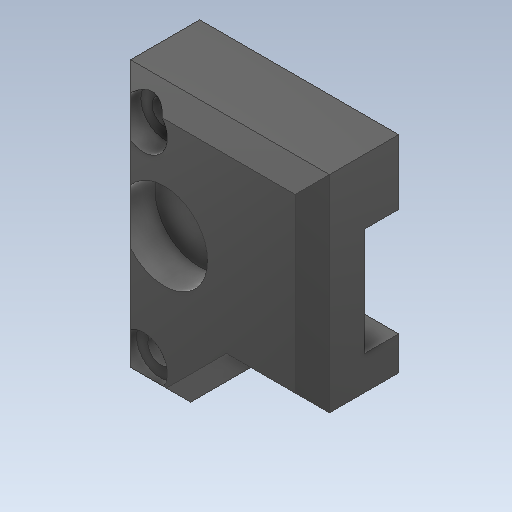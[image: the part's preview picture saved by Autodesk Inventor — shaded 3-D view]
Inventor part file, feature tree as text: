
AUTODESK INVENTOR PART (.ipt)
format: ipt  version: 2020 (Build 240168000, 168)  size: 249,856 bytes
history: native  units: in
note: dims shown in document units (in); Inventor stores cm internally (conversion verified against a paired STEP export)
features: sketch x30, other x3, plane x1
ambient origin geometry x8: Origin, YZ Plane, XZ Plane, XY Plane, X Axis, Y Axis, Z Axis, Center Point
bodies: Solid1 (feature_tree)
feature tree (34):
  other  "FermurSupportSup.ipt"
  other  "Solid1::FermurSupportSup.ipt"
  other  "TaggingFeature1"
  sketch  "Sketch1"  dims[d0=0.3937in]
  sketch  "Sketch2"
  sketch  "Sketch3"
  sketch  "Sketch4"
  sketch  "Sketch5"
  sketch  "Sketch6"
  sketch  "Sketch8"
  sketch  "Sketch10"
  sketch  "Sketch11"
  sketch  "Sketch12"
  sketch  "Sketch13"
  sketch  "Sketch14"
  sketch  "Sketch15"
  sketch  "Sketch17"
  sketch  "Sketch19"
  sketch  "Sketch21"
  sketch  "Sketch22"
  sketch  "Sketch23"
  sketch  "Sketch24"
  sketch  "Sketch25"
  sketch  "Sketch26"
  sketch  "Sketch27"
  sketch  "Sketch29"
  sketch  "Sketch32"
  sketch  "Sketch33"
  sketch  "Sketch36"
  sketch  "Sketch37"
  sketch  "Sketch38"
  sketch  "Sketch39"
  sketch  "Sketch40"
  plane  "Work Plane1"
